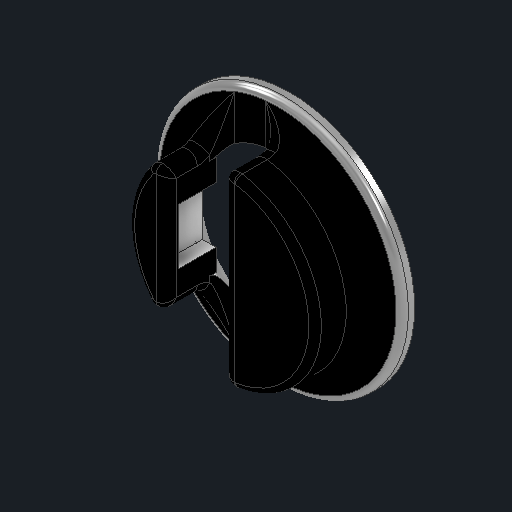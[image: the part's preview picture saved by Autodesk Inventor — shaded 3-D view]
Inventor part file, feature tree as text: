
AUTODESK INVENTOR PART (.ipt)
format: ipt  version: 2023 (Build 270158000, 158)  size: 415,232 bytes
history: native  units: mm
features: fillet x8, extrude x6, sketch x5
ambient origin geometry x8: Origin, YZ Plane, XZ Plane, XY Plane, X Axis, Y Axis, Z Axis, Center Point
bodies: Solid1 (feature_tree)
feature tree (19):
  extrude  "Extrusion1"  Depth=10.0mm TaperAngle=0.0deg
  extrude  "Extrusion2"  Depth=5.0mm TaperAngle=0.0deg
  fillet  "Fillet1"  Radius=20.0mm
  fillet  "Fillet2"  Radius=5.0mm
  fillet  "Fillet3"  Radius=5.0mm
  extrude  "Extrusion3"  Depth=45.0mm TaperAngle=0.0deg
  fillet  "Fillet4"  Radius=20.0mm
  extrude  "Extrusion4"  Depth=45.0mm
  sketch  "Sketch5"  dims[d15=30.0mm d16=0.0mm d17=30.0mm d18=0.0mm d19=35.0mm d20=0.0mm d21=10.0mm d22=5.0mm d23=10.0mm d24=8.0mm]
  extrude  "Extrusion5"  Depth=5.0mm TaperAngle=0.0deg
  extrude  "Extrusion6"  Depth=5.0mm TaperAngle=0.0deg
  fillet  "Fillet5"  Radius=10.0mm
  fillet  "Fillet6"  Radius=5.0mm
  fillet  "Fillet7"  Radius=10.0mm
  fillet  "Fillet8"  Radius=8.0mm
  sketch  "Sketch1"  dims[d0=200.0mm d1=10.0mm d2=0.0mm]
  sketch  "Sketch2"  dims[d3=150.0mm d4=45.0mm d5=0.0mm d6=20.0mm d7=5.0mm d8=5.0mm]
  sketch  "Sketch3"  dims[d9=15.0mm d10=45.0mm d11=0.0mm d12=20.0mm]
  sketch  "Sketch4"  dims[d13=22.5mm d14=45.0mm]
